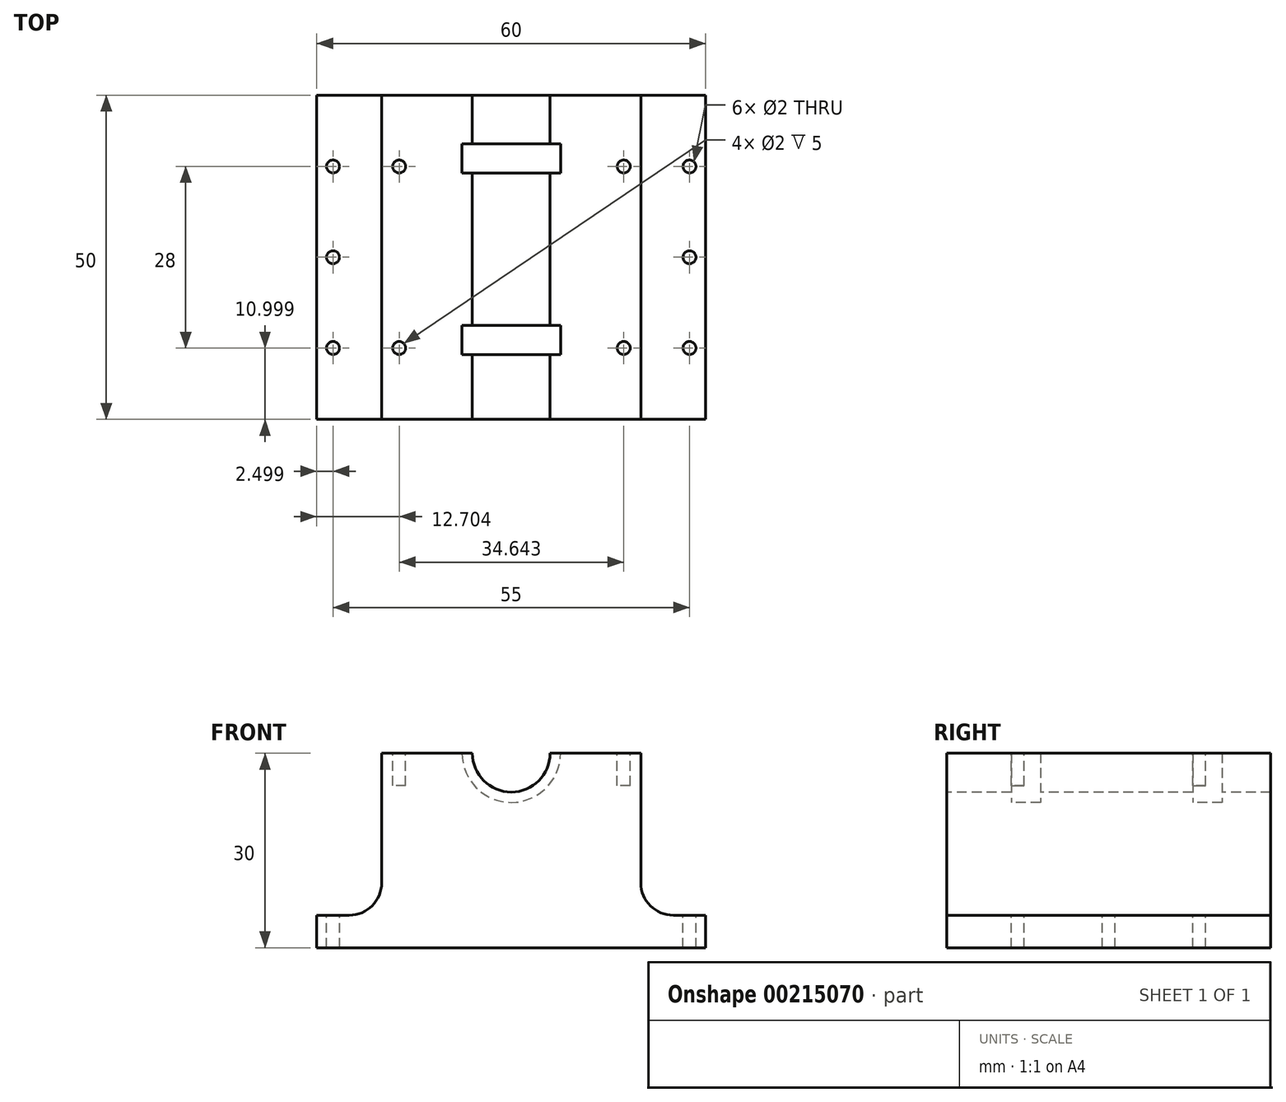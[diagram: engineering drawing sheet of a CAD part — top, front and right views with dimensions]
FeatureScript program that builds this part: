
annotation { "Feature Type Name" : "Feature", "Feature Type Description" : "" }
export const myFeature = defineFeature(function(context is Context, id is Id, definition is map)
    precondition{}
    {
        {
            var Q0;
            Q0=qCreatedBy(makeId("Top.planeOp"),FACE);
            var sketch = newSketch(context, id + "F0", { "sketchPlane" : qUnion([Q0])});
            skLineSegment(sketch, "E0.bottom", {"start": v(-38.4, 4.47) * mm, "end": v(21.6, 4.47) * mm});
            skLineSegment(sketch, "E0.top", {"start": v(-38.4, 54.47) * mm, "end": v(21.6, 54.47) * mm});
            skLineSegment(sketch, "E0.left", {"start": v(-38.4, 4.47) * mm, "end": v(-38.4, 54.47) * mm});
            skLineSegment(sketch, "E0.right", {"start": v(21.6, 4.47) * mm, "end": v(21.6, 54.47) * mm});
            skSolve(sketch);
        }
        {
            var Q0;
            Q0 = qSketchRegion(id + "F0", true);
            extrude(context, id + "F1", {"entities" : qUnion([Q0]), "depth" : 30 * mm});
        }
        {
            var Q0;
            Q0=makeQuery(id+"F1.opExtrude","CAP_FACE",FACE,{"disambiguationData":[OSD([sQuery(id+"F0.wireOp",EDGE,"E0.bottom"),sQuery(id+"F0.wireOp",EDGE,"E0.top"),sQuery(id+"F0.wireOp",EDGE,"E0.left"),sQuery(id+"F0.wireOp",EDGE,"E0.right")])],"isStart":false});
            var sketch = newSketch(context, id + "F2", { "sketchPlane" : qUnion([Q0])});
            skLineSegment(sketch, "E1", {"start": v(-8.4, 4.47) * mm, "end": v(-8.4, 54.47) * mm, "construction": true});
            skSolve(sketch);
        }
        {
            var Q0;
            Q0=makeQuery(id+"F1.opExtrude","SWEPT_FACE",FACE,{"disambiguationData":[OSD([sQuery(id+"F0.wireOp",EDGE,"E0.bottom")])]});
            var sketch = newSketch(context, id + "F3", { "sketchPlane" : qUnion([Q0])});
            skLineSegment(sketch, "E2", {"start": v(-8.4, 30) * mm, "end": v(-8.4, 0) * mm, "construction": true});
            skCircle(sketch, "E3", {"center": v(-8.4, 30) * mm, "radius": 6 * mm});
            skLineSegment(sketch, "E4.top", {"start": v(-28.4, 0) * mm, "end": v(11.6, 0) * mm, "construction": true});
            skLineSegment(sketch, "E5.right", {"start": v(-28.4, 30) * mm, "end": v(-28.4, 10) * mm});
            skLineSegment(sketch, "E6.left", {"start": v(21.6, 30) * mm, "end": v(21.6, 5) * mm});
            skLineSegment(sketch, "E6.right", {"start": v(11.6, 30) * mm, "end": v(11.6, 10) * mm});
            skLineSegment(sketch, "E7", {"start": v(21.6, 5) * mm, "end": v(16.6, 5) * mm});
            skArc(sketch, "E8.filletArc", {"start": v(11.6, 10) * mm, "mid": v(13.07, 6.46) * mm, "end": v(16.6, 5) * mm});
            skArc(sketch, "E9.MirrorCS", {"start": v(-28.4, 10) * mm, "mid": v(-29.85, 6.46) * mm, "end": v(-33.4, 5) * mm});
            skLineSegment(sketch, "E10.MirrorCS", {"start": v(-38.4, 5) * mm, "end": v(-33.4, 5) * mm});
            skLineSegment(sketch, "E11", {"start": v(-28.4, 30) * mm, "end": v(-38.4, 30) * mm});
            skLineSegment(sketch, "E12", {"start": v(-38.4, 30) * mm, "end": v(-38.4, 5) * mm});
            skLineSegment(sketch, "E13", {"start": v(11.6, 30) * mm, "end": v(21.6, 30) * mm});
            skPoint(sketch, "E14.orphan", {"position": v(21.6, 0) * mm});
            skSolve(sketch);
        }
        {
            var Q0;
            Q0 = qSketchRegion(id + "F3", true);
            extrude(context, id + "F4", {"entities" : qUnion([Q0]), "operationType" : NewBodyOperationType.REMOVE, "oppositeDirection" : true, "depth" : 90 * mm});
        }
        {
            var Q0;
            Q0=makeQuery(id+"F1.opExtrude","SWEPT_FACE",FACE,{"disambiguationData":[OSD([sQuery(id+"F0.wireOp",EDGE,"E0.bottom")])]});
            cPlane(context, id + "F5", {"entities" : qUnion([Q0]), "cplaneType" : CPlaneType.OFFSET, "offset" : 10 * mm, "oppositeDirection" : true, "width" : 150 * mm, "height" : 150 * mm});
        }
        {
            var Q0;
            Q0=qCreatedBy(id+"F5.planeOp",FACE);
            var sketch = newSketch(context, id + "F6", { "sketchPlane" : qUnion([Q0])});
            skCircle(sketch, "E15", {"center": v(-8.4, 30) * mm, "radius": 7.6 * mm});
            skSolve(sketch);
        }
        {
            var Q0;
            Q0 = qSketchRegion(id + "F6", true);
            extrude(context, id + "F7", {"entities" : qUnion([Q0]), "operationType" : NewBodyOperationType.REMOVE, "oppositeDirection" : true, "depth" : 4.5 * mm});
        }
        {
            var Q0;
            Q0 = qSketchRegion(id + "F6", true);
            extrude(context, id + "F8", {"entities" : qUnion([Q0]), "operationType" : NewBodyOperationType.REMOVE, "oppositeDirection" : true, "depth" : 32.5 * mm, "hasSecondDirection" : true, "secondDirectionOppositeDirection" : true, "secondDirectionDepth" : 28 * mm});
        }
        {
            var Q0;
            Q0=makeQuery(id+"F2.imprint","IMPRINT",FACE,{"disambiguationData":[TD([[makeQuery(id+"F2.imprint","IMPRINT",EDGE,{"derivedFrom":makeQuery(id+"F1.opExtrude","CAP_EDGE",EDGE,{"disambiguationData":[OSD([sQuery(id+"F0.wireOp",EDGE,"E0.bottom")])],"isStart":false})}),1.0]])]});
            cPlane(context, id + "F9", {"entities" : qUnion([Q0]), "cplaneType" : CPlaneType.OFFSET, "offset" : 10 * mm, "width" : 150 * mm, "height" : 150 * mm});
        }
        {
            var Q0;
            Q0=makeQuery(id+"F4.boolean.opBoolean","COPY",FACE,{"derivedFrom":makeQuery(id+"F4.opExtrude","SWEPT_FACE",FACE,{"disambiguationData":[OSD([sQuery(id+"F3.wireOp",EDGE,"E7")])]})});
            var sketch = newSketch(context, id + "F10", { "sketchPlane" : qUnion([Q0])});
            skLineSegment(sketch, "E16", {"start": v(19.1, 4.47) * mm, "end": v(19.1, 54.47) * mm, "construction": true});
            skCircle(sketch, "E17", {"center": v(19.1, 15.47) * mm, "radius": 1 * mm});
            skCircle(sketch, "E18", {"center": v(19.1, 43.47) * mm, "radius": 1 * mm});
            skCircle(sketch, "E19", {"center": v(19.1, 29.47) * mm, "radius": 1 * mm});
            skCircle(sketch, "E20.MirrorC", {"center": v(-35.9, 15.47) * mm, "radius": 1 * mm});
            skCircle(sketch, "E21.MirrorC", {"center": v(-35.9, 29.47) * mm, "radius": 1 * mm});
            skCircle(sketch, "E22.MirrorC", {"center": v(-35.9, 43.47) * mm, "radius": 1 * mm});
            skSolve(sketch);
        }
        {
            var Q0;
            Q0 = qSketchRegion(id + "F10", true);
            extrude(context, id + "F11", {"entities" : qUnion([Q0]), "operationType" : NewBodyOperationType.REMOVE, "oppositeDirection" : true, "depth" : 25 * mm});
        }
        {
            var Q0;
            {var subQ0=sQuery(id+"F0.wireOp",EDGE,"E0.bottom");var subQ1=sQuery(id+"F0.wireOp",EDGE,"E0.top");Q0=makeQuery(id+"F4.boolean.opBoolean","SPLIT",FACE,{"disambiguationData":[TD([makeQuery(id+"F4.opExtrude","SWEPT_FACE",FACE,{"disambiguationData":[OSD([sQuery(id+"F3.wireOp",EDGE,"E6.right")])]})])],"derivedFrom":makeQuery(id+"F1.opExtrude","CAP_FACE",FACE,{"disambiguationData":[OSD([subQ0,subQ1,sQuery(id+"F0.wireOp",EDGE,"E0.left"),sQuery(id+"F0.wireOp",EDGE,"E0.right")])],"isStart":false})});}
            var sketch = newSketch(context, id + "F12", { "sketchPlane" : qUnion([Q0])});
            skCircle(sketch, "E23", {"center": v(8.96, 43.47) * mm, "radius": 1 * mm});
            skLineSegment(sketch, "E24", {"start": v(11.6, 4.47) * mm, "end": v(11.6, 54.47) * mm, "construction": true});
            skPoint(sketch, "E25.endSnap0", {"position": v(-2.4, 30.72) * mm});
            skPoint(sketch, "E26.endSnap0", {"position": v(-8.36, 30.1) * mm});
            skPoint(sketch, "E27.endSnap0", {"position": v(11.6, 29.47) * mm});
            skLineSegment(sketch, "E28", {"start": v(11.6, 29.47) * mm, "end": v(-28.4, 29.47) * mm, "construction": true});
            skLineSegment(sketch, "E29", {"start": v(-8.36, 29.47) * mm, "end": v(-8.36, 4.33) * mm, "construction": true});
            skPoint(sketch, "E29.startSnap0", {"position": v(-8.4, 29.47) * mm});
            skCircle(sketch, "E30.MirrorC", {"center": v(8.96, 15.47) * mm, "radius": 1 * mm});
            skLineSegment(sketch, "E31.MirrorCS", {"start": v(-8.36, 29.47) * mm, "end": v(-8.36, 54.61) * mm, "construction": true});
            skCircle(sketch, "E32.MirrorC", {"center": v(-25.69, 15.47) * mm, "radius": 1 * mm});
            skCircle(sketch, "E33.MirrorC", {"center": v(-25.69, 43.47) * mm, "radius": 1 * mm});
            skSolve(sketch);
        }
        {
            var Q0;
            Q0 = qSketchRegion(id + "F12", true);
            extrude(context, id + "F13", {"entities" : qUnion([Q0]), "operationType" : NewBodyOperationType.REMOVE, "oppositeDirection" : true, "depth" : 5 * mm});
        }
    });
